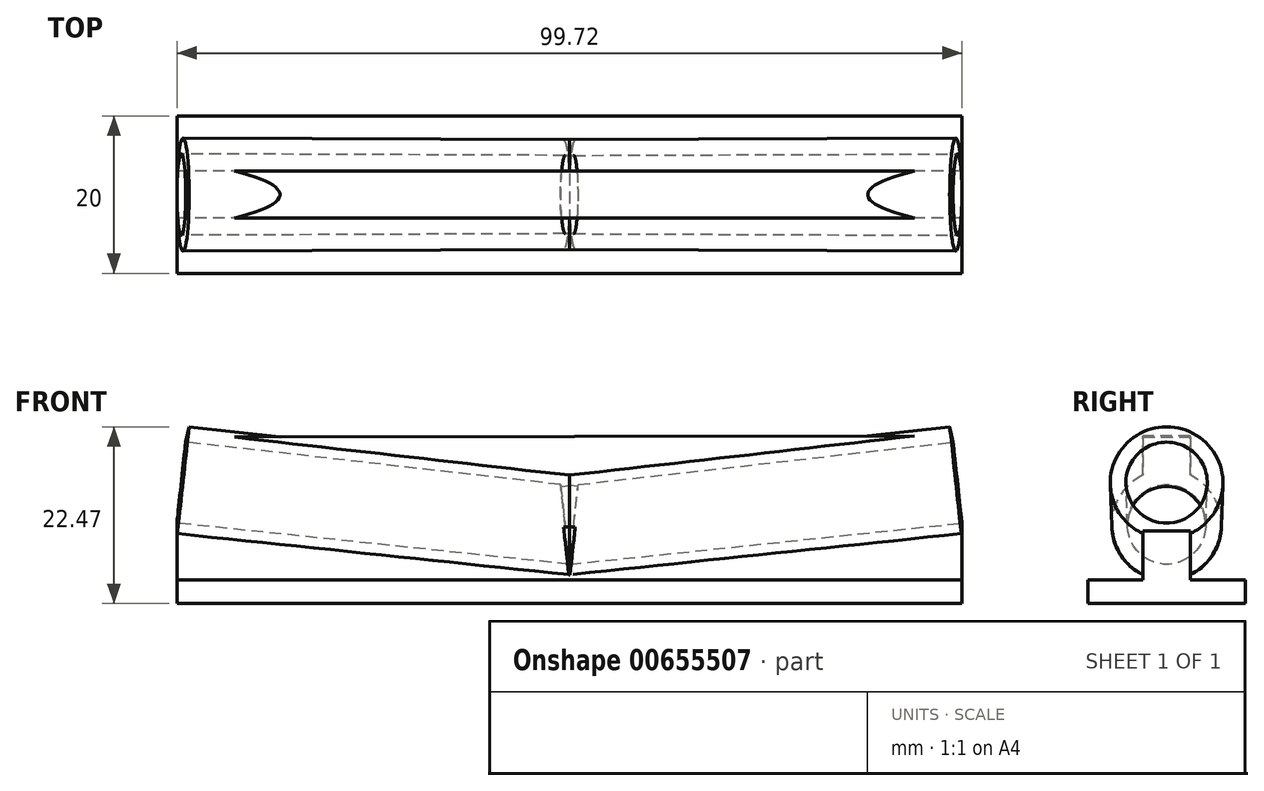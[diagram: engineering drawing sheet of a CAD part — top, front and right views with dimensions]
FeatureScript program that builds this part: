
annotation { "Feature Type Name" : "Feature", "Feature Type Description" : "" }
export const myFeature = defineFeature(function(context is Context, id is Id, definition is map)
    precondition{}
    {
        {
            var Q0;
            Q0=qCreatedBy(makeId("Front.planeOp"),FACE);
            var sketch = newSketch(context, id + "F0", { "sketchPlane" : qUnion([Q0])});
            skLineSegment(sketch, "E0", {"start": v(0, 0) * mm, "end": v(49.86, 0) * mm});
            skLineSegment(sketch, "E1", {"start": v(0, 0) * mm, "end": v(49.86, 5.24) * mm});
            skLineSegment(sketch, "E2", {"start": v(0, 0) * mm, "end": v(0, 0) * mm});
            skLineSegment(sketch, "E3", {"start": v(0, 0) * mm, "end": v(0, 2) * mm});
            skLineSegment(sketch, "E4", {"start": v(49.86, 5.24) * mm, "end": v(49.86, 7.24) * mm});
            skLineSegment(sketch, "E5", {"start": v(0, 2) * mm, "end": v(49.86, 7.24) * mm});
            skLineSegment(sketch, "E6", {"start": v(49.86, 7.24) * mm, "end": v(49.86, 12.44) * mm});
            skLineSegment(sketch, "E7", {"start": v(0, 2) * mm, "end": v(0, 7) * mm});
            skLineSegment(sketch, "E8", {"start": v(0, 7) * mm, "end": v(49.86, 12.44) * mm});
            skLineSegment(sketch, "E9", {"start": v(49.86, 0) * mm, "end": v(49.86, 5.24) * mm});
            skLineSegment(sketch, "E10", {"start": v(0, -3) * mm, "end": v(0, 0) * mm});
            skLineSegment(sketch, "E11", {"start": v(49.86, -3) * mm, "end": v(49.86, 0) * mm});
            skLineSegment(sketch, "E12", {"start": v(0, -3) * mm, "end": v(49.86, -3) * mm});
            skLineSegment(sketch, "E13.MirrorCS", {"start": v(0, 7) * mm, "end": v(-49.86, 12.44) * mm});
            skLineSegment(sketch, "E14.MirrorCS", {"start": v(-49.86, 7.24) * mm, "end": v(-49.86, 12.44) * mm});
            skLineSegment(sketch, "E15.MirrorCS", {"start": v(0, 0) * mm, "end": v(-49.86, 5.24) * mm});
            skLineSegment(sketch, "E16.MirrorCS", {"start": v(0, 2) * mm, "end": v(-49.86, 7.24) * mm});
            skLineSegment(sketch, "E17.MirrorCS", {"start": v(-49.86, 0) * mm, "end": v(-49.86, 5.24) * mm});
            skLineSegment(sketch, "E18.MirrorCS", {"start": v(0, -3) * mm, "end": v(-49.86, -3) * mm});
            skLineSegment(sketch, "E19.MirrorCS", {"start": v(0, 0) * mm, "end": v(-49.86, 0) * mm});
            skLineSegment(sketch, "E20.MirrorCS", {"start": v(-49.86, -3) * mm, "end": v(-49.86, 0) * mm});
            skLineSegment(sketch, "E21.MirrorCS", {"start": v(-49.86, 5.24) * mm, "end": v(-49.86, 7.24) * mm});
            skLineSegment(sketch, "E22", {"start": v(0, 1) * mm, "end": v(-49.86, 6.24) * mm});
            skLineSegment(sketch, "E23.MirrorCS", {"start": v(0, 1) * mm, "end": v(49.86, 6.24) * mm});
            skSolve(sketch);
        }
        {
            var Q0;
            Q0=makeQuery(id+"F0.imprint","IMPRINT",FACE,{"disambiguationData":[TD([[makeQuery(id+"F0.imprint","IMPRINT",EDGE,{"derivedFrom":sQuery(id+"F0.wireOp",EDGE,"E3")}),1.0]])]});
            var Q1;
            Q1=sQuery(id+"F0.wireOp",EDGE,"E13.MirrorCS");
            revolve(context, id + "F1", {"entities" : qUnion([Q0]), "axis" : qUnion([Q1]), "revolveType" : RevolveType.FULL});
        }
        {
            var Q0;
            Q0=makeQuery(id+"F0.imprint","IMPRINT",FACE,{"disambiguationData":[TD([[makeQuery(id+"F0.imprint","IMPRINT",EDGE,{"derivedFrom":sQuery(id+"F0.wireOp",EDGE,"E1")}),1.0]])]});
            var Q1;
            {var subQ0=sQuery(id+"F0.wireOp",EDGE,"E5");Q1=makeQuery(id+"F0.imprint","IMPRINT",FACE,{"disambiguationData":[TD([[makeQuery(id+"F0.imprint","IMPRINT",EDGE,{"derivedFrom":subQ0}),-1.0]])]});}
            var Q2;
            Q2=sQuery(id+"F0.wireOp",EDGE,"E8");
            revolve(context, id + "F2", {"operationType" : NewBodyOperationType.ADD, "entities" : qUnion([Q0, Q1]), "axis" : qUnion([Q2]), "revolveType" : RevolveType.FULL});
        }
        {
            var Q0;
            Q0=makeQuery(id+"F0.imprint","IMPRINT",FACE,{"disambiguationData":[TD([[makeQuery(id+"F0.imprint","IMPRINT",EDGE,{"derivedFrom":sQuery(id+"F0.wireOp",EDGE,"E15.MirrorCS")}),1.0]])]});
            var Q1;
            Q1=makeQuery(id+"F0.imprint","IMPRINT",FACE,{"disambiguationData":[TD([[makeQuery(id+"F0.imprint","IMPRINT",EDGE,{"derivedFrom":sQuery(id+"F0.wireOp",EDGE,"E0")}),1.0]])]});
            var Q2;
            {var subQ0=sQuery(id+"F0.wireOp",EDGE,"E15.MirrorCS");Q2=makeQuery(id+"F0.imprint","IMPRINT",FACE,{"disambiguationData":[TD([[makeQuery(id+"F0.imprint","IMPRINT",EDGE,{"derivedFrom":subQ0}),-1.0]])]});}
            var Q3;
            {var subQ0=sQuery(id+"F0.wireOp",EDGE,"E1");Q3=makeQuery(id+"F0.imprint","IMPRINT",FACE,{"disambiguationData":[TD([[makeQuery(id+"F0.imprint","IMPRINT",EDGE,{"derivedFrom":subQ0}),1.0]])]});}
            extrude(context, id + "F3", {"entities" : qUnion([Q0, Q1, Q2, Q3]), "operationType" : NewBodyOperationType.ADD, "endBound" : BoundingType.SYMMETRIC, "depth" : 6 * mm, "offsetDistance" : 25 * mm});
        }
        {
            var Q0;
            Q0=makeQuery(id+"F0.imprint","IMPRINT",FACE,{"disambiguationData":[TD([[makeQuery(id+"F0.imprint","IMPRINT",EDGE,{"derivedFrom":sQuery(id+"F0.wireOp",EDGE,"E10")}),1.0]])]});
            var Q1;
            Q1=makeQuery(id+"F0.imprint","IMPRINT",FACE,{"disambiguationData":[TD([[makeQuery(id+"F0.imprint","IMPRINT",EDGE,{"derivedFrom":sQuery(id+"F0.wireOp",EDGE,"E0")}),-1.0]])]});
            extrude(context, id + "F4", {"entities" : qUnion([Q0, Q1]), "operationType" : NewBodyOperationType.ADD, "endBound" : BoundingType.SYMMETRIC, "depth" : 20 * mm, "offsetDistance" : 25 * mm});
        }
        {
            var Q0;
            Q0=qCreatedBy(makeId("Front.planeOp"),FACE);
            var sketch = newSketch(context, id + "F5", { "sketchPlane" : qUnion([Q0])});
            skPoint(sketch, "E24", {"position": v(0, 13.05) * mm});
            skPoint(sketch, "E25", {"position": v(48.4, 18.31) * mm});
            skPoint(sketch, "E26", {"position": v(-48.5, 18.14) * mm});
            skLineSegment(sketch, "E27", {"start": v(-48.5, 18.14) * mm, "end": v(48.4, 18.31) * mm});
            skLineSegment(sketch, "E28", {"start": v(0, 13.05) * mm, "end": v(-48.5, 18.14) * mm});
            skLineSegment(sketch, "E29", {"start": v(0, 13.05) * mm, "end": v(48.4, 18.31) * mm});
            skSolve(sketch);
        }
        {
            var Q0;
            Q0=makeQuery(id+"F5.imprint","IMPRINT",FACE,{"disambiguationData":[TD([[makeQuery(id+"F5.imprint","IMPRINT",EDGE,{"derivedFrom":sQuery(id+"F5.wireOp",EDGE,"E27")}),-1.0]])]});
            extrude(context, id + "F6", {"entities" : qUnion([Q0]), "operationType" : NewBodyOperationType.ADD, "endBound" : BoundingType.SYMMETRIC, "depth" : 6 * mm, "offsetDistance" : 25 * mm});
        }
    });
